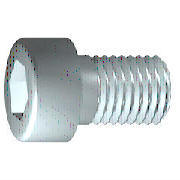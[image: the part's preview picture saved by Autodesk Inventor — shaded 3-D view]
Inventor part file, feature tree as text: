
AUTODESK INVENTOR PART (.ipt)
format: ipt  version: 2022 (Build 260153000, 153)  size: 202,240 bytes
history: native  units: mm (DEFAULTED — no unit token found)
features: sketch x2, other x1, extrude x1, plane x1, fillet x1
ambient origin geometry x7: Origin, YZ Plane, XY Plane, X Axis, Y Axis, Z Axis, Center Point
bodies: Solid1 (feature_tree)
feature tree (6):
  other  "Cuerpo"
  extrude  "Ranura"  Depth=1.6mm
  plane  "Work Plane1"
  fillet  "Fillet2"  Radius=1.6mm
  sketch  "Boceto1"  dims[d1=1.625mm d2=0.214807mm d3=1.6mm]
  sketch  "Boceto2"  dims[d4=0.7mm d5=60.0deg d6=1.6mm d7=1.6mm d8=1.732051mm d9=3.0mm d10=90.0deg d11=10.0mm d12=0.0mm d13=1.625mm d14=0.0mm d15=0.214707mm d16=0.214707mm d17=0.16mm d19=0.0mm d26=2.5mm d27=45.0deg d28=0.0mm d29=0.0mm d30=0.1mm]
